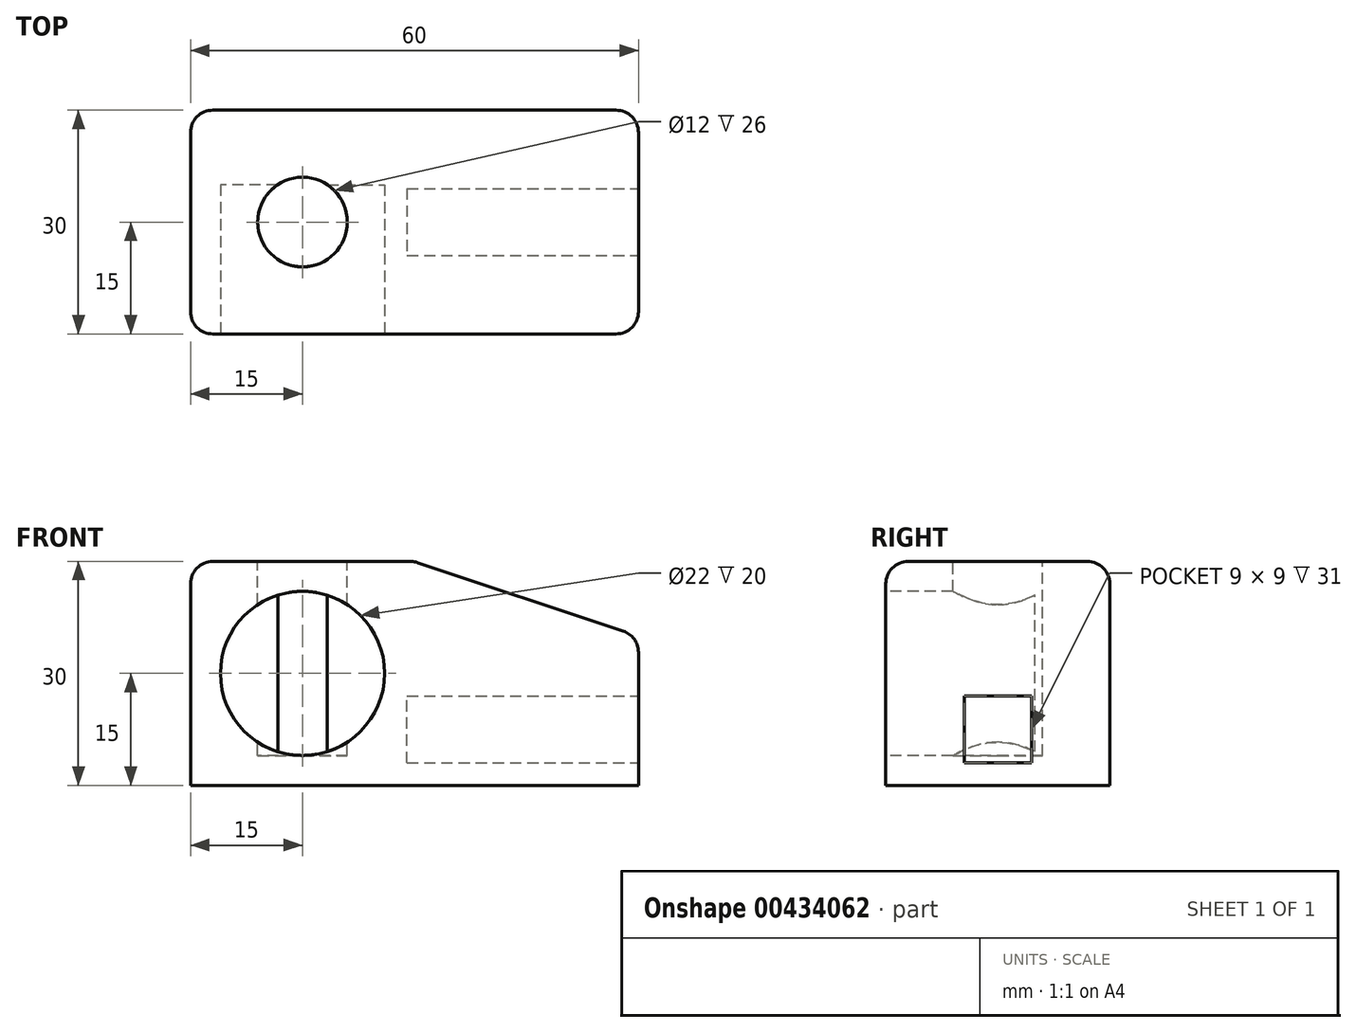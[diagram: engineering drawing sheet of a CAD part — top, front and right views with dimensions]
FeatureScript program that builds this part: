
annotation { "Feature Type Name" : "Feature", "Feature Type Description" : "" }
export const myFeature = defineFeature(function(context is Context, id is Id, definition is map)
    precondition{}
    {
        {
            var Q0;
            Q0=qCreatedBy(makeId("Front.planeOp"),FACE);
            var sketch = newSketch(context, id + "F0", { "sketchPlane" : qUnion([Q0])});
            skLineSegment(sketch, "E0.bottom", {"start": v(30, -15) * mm, "end": v(-30, -15) * mm});
            skLineSegment(sketch, "E0.top", {"start": v(30, 15) * mm, "end": v(-30, 15) * mm});
            skLineSegment(sketch, "E0.left", {"start": v(30, -15) * mm, "end": v(30, 15) * mm});
            skLineSegment(sketch, "E0.right", {"start": v(-30, -15) * mm, "end": v(-30, 15) * mm});
            skPoint(sketch, "E0.middle", {"position": v(0, 0) * mm});
            skSolve(sketch);
        }
        {
            var Q0;
            Q0=makeQuery(id+"F0.imprint","IMPRINT",FACE,{"disambiguationData":[TD([[makeQuery(id+"F0.imprint","IMPRINT",EDGE,{"derivedFrom":sQuery(id+"F0.wireOp",EDGE,"E0.bottom")}),-1.0]])]});
            extrude(context, id + "F1", {"entities" : qUnion([Q0]), "depth" : 30 * mm});
        }
        {
            var Q0;
            Q0=makeQuery(id+"F1.opExtrude","CAP_FACE",FACE,{"disambiguationData":[OSD([sQuery(id+"F0.wireOp",EDGE,"E0.bottom"),sQuery(id+"F0.wireOp",EDGE,"E0.top"),sQuery(id+"F0.wireOp",EDGE,"E0.left"),sQuery(id+"F0.wireOp",EDGE,"E0.right")])],"isStart":false});
            var sketch = newSketch(context, id + "F2", { "sketchPlane" : qUnion([Q0])});
            skLineSegment(sketch, "E1", {"start": v(0, 0) * mm, "end": v(-15, 0) * mm, "construction": true});
            skCircle(sketch, "E2", {"center": v(-15, 0) * mm, "radius": 11 * mm});
            skSolve(sketch);
        }
        {
            var Q0;
            Q0=makeQuery(id+"F2.imprint","IMPRINT",FACE,{"disambiguationData":[TD([[makeQuery(id+"F2.imprint","IMPRINT",EDGE,{"derivedFrom":sQuery(id+"F2.wireOp",EDGE,"E2")}),1.0]])]});
            extrude(context, id + "F3", {"entities" : qUnion([Q0]), "operationType" : NewBodyOperationType.REMOVE, "oppositeDirection" : true, "depth" : 20 * mm});
        }
        {
            var Q0;
            Q0=makeQuery(id+"F1.opExtrude","SWEPT_FACE",FACE,{"disambiguationData":[OSD([sQuery(id+"F0.wireOp",EDGE,"E0.left")])]});
            var sketch = newSketch(context, id + "F4", { "sketchPlane" : qUnion([Q0])});
            skLineSegment(sketch, "E3", {"start": v(-30, -12) * mm, "end": v(0, -12) * mm, "construction": true});
            skLineSegment(sketch, "E4", {"start": v(-15, 15) * mm, "end": v(-15, -15) * mm, "construction": true});
            skLineSegment(sketch, "E5", {"start": v(-19.5, 15) * mm, "end": v(-19.5, -15) * mm, "construction": true});
            skLineSegment(sketch, "E6", {"start": v(-10.5, 15) * mm, "end": v(-10.5, -15) * mm, "construction": true});
            skLineSegment(sketch, "E7", {"start": v(-30, -3) * mm, "end": v(0, -3) * mm, "construction": true});
            skLineSegment(sketch, "E8", {"start": v(-19.5, -12) * mm, "end": v(-19.5, -3) * mm});
            skLineSegment(sketch, "E9", {"start": v(-19.5, -3) * mm, "end": v(-10.5, -3) * mm});
            skLineSegment(sketch, "E10", {"start": v(-10.5, -3) * mm, "end": v(-10.5, -12) * mm});
            skLineSegment(sketch, "E11", {"start": v(-10.5, -12) * mm, "end": v(-19.5, -12) * mm});
            skSolve(sketch);
        }
        {
            var Q0;
            Q0=makeQuery(id+"F4.imprint","IMPRINT",FACE,{"disambiguationData":[TD([[makeQuery(id+"F4.imprint","IMPRINT",EDGE,{"derivedFrom":sQuery(id+"F4.wireOp",EDGE,"E8")}),-1.0]])]});
            extrude(context, id + "F5", {"entities" : qUnion([Q0]), "operationType" : NewBodyOperationType.REMOVE, "oppositeDirection" : true, "depth" : 31 * mm});
        }
        {
            var Q0;
            Q0=makeQuery(id+"F1.opExtrude","SWEPT_FACE",FACE,{"disambiguationData":[OSD([sQuery(id+"F0.wireOp",EDGE,"E0.top")])]});
            var sketch = newSketch(context, id + "F6", { "sketchPlane" : qUnion([Q0])});
            skLineSegment(sketch, "E12", {"start": v(-30, 0) * mm, "end": v(0, -30) * mm, "construction": true});
            skLineSegment(sketch, "E13", {"start": v(0, -30) * mm, "end": v(0, 0) * mm, "construction": true});
            skLineSegment(sketch, "E14", {"start": v(0, 0) * mm, "end": v(-30, -30) * mm, "construction": true});
            skPoint(sketch, "E15", {"position": v(-15, -15) * mm});
            skCircle(sketch, "E16", {"center": v(-15, -15) * mm, "radius": 6 * mm});
            skSolve(sketch);
        }
        {
            var Q0;
            Q0=makeQuery(id+"F6.imprint","IMPRINT",FACE,{"disambiguationData":[TD([[makeQuery(id+"F6.imprint","IMPRINT",EDGE,{"derivedFrom":sQuery(id+"F6.wireOp",EDGE,"E16")}),1.0]])]});
            extrude(context, id + "F7", {"entities" : qUnion([Q0]), "operationType" : NewBodyOperationType.REMOVE, "oppositeDirection" : true, "depth" : 26 * mm});
        }
        {
            var Q0;
            Q0=makeQuery(id+"F1.opExtrude","SWEPT_EDGE",EDGE,{"disambiguationData":[OSD([sQuery(id+"F0.wireOp",EDGE,"E0.top"),sQuery(id+"F0.wireOp",EDGE,"E0.left")])]});
            chamfer(context, id + "F8", {"entities" : qUnion([Q0]), "chamferType" : ChamferType.TWO_OFFSETS, "width1" : 30 * mm, "oppositeDirection" : false, "width2" : 10 * mm, "tangentPropagation" : true});
        }
        {
            var Q0;
            Q0=makeQuery(id+"F1.opExtrude","SWEPT_EDGE",EDGE,{"disambiguationData":[OSD([sQuery(id+"F0.wireOp",EDGE,"E0.top"),sQuery(id+"F0.wireOp",EDGE,"E0.right")])]});
            var Q1;
            Q1=makeQuery(id+"F1.opExtrude","CAP_EDGE",EDGE,{"disambiguationData":[OSD([sQuery(id+"F0.wireOp",EDGE,"E0.top")])],"isStart":true});
            var Q2;
            {var subQ0=sQuery(id+"F0.wireOp",EDGE,"E0.top");Q2=makeQuery(id+"F8.opChamfer","BLEND_EDGE",EDGE,{"blendedFrom":[makeQuery(id+"F1.opExtrude","SWEPT_EDGE",EDGE,{"disambiguationData":[OSD([subQ0,sQuery(id+"F0.wireOp",EDGE,"E0.left")])]}),makeQuery(id+"F1.opExtrude","SWEPT_FACE",FACE,{"disambiguationData":[OSD([subQ0])]})],"blendedInto":[makeQuery(id+"F1.opExtrude","SWEPT_FACE",FACE,{"disambiguationData":[OSD([subQ0])]})]});}
            var Q3;
            {var subQ0=sQuery(id+"F0.wireOp",EDGE,"E0.left");Q3=makeQuery(id+"F8.opChamfer","BLEND_EDGE",EDGE,{"blendedFrom":[makeQuery(id+"F1.opExtrude","SWEPT_EDGE",EDGE,{"disambiguationData":[OSD([sQuery(id+"F0.wireOp",EDGE,"E0.top"),subQ0])]}),makeQuery(id+"F1.opExtrude","SWEPT_FACE",FACE,{"disambiguationData":[OSD([subQ0])]})],"blendedInto":[makeQuery(id+"F1.opExtrude","SWEPT_FACE",FACE,{"disambiguationData":[OSD([subQ0])]})]});}
            var Q4;
            Q4=makeQuery(id+"F1.opExtrude","CAP_EDGE",EDGE,{"disambiguationData":[OSD([sQuery(id+"F0.wireOp",EDGE,"E0.top")])],"isStart":false});
            var Q5;
            {var subQ0=sQuery(id+"F0.wireOp",EDGE,"E0.left");var subQ1=sQuery(id+"F0.wireOp",EDGE,"E0.top");Q5=makeQuery(id+"F8.opChamfer","BLEND_EDGE",EDGE,{"blendedFrom":[makeQuery(id+"F1.opExtrude","SWEPT_EDGE",EDGE,{"disambiguationData":[OSD([subQ1,subQ0])]}),makeQuery(id+"F1.opExtrude","CAP_FACE",FACE,{"disambiguationData":[OSD([sQuery(id+"F0.wireOp",EDGE,"E0.bottom"),subQ1,subQ0,sQuery(id+"F0.wireOp",EDGE,"E0.right")])],"isStart":false})],"blendedInto":[makeQuery(id+"F1.opExtrude","CAP_FACE",FACE,{"disambiguationData":[OSD([sQuery(id+"F0.wireOp",EDGE,"E0.bottom"),subQ1,subQ0,sQuery(id+"F0.wireOp",EDGE,"E0.right")])],"isStart":false})]});}
            var Q6;
            {var subQ0=sQuery(id+"F0.wireOp",EDGE,"E0.left");var subQ1=sQuery(id+"F0.wireOp",EDGE,"E0.top");Q6=makeQuery(id+"F8.opChamfer","BLEND_EDGE",EDGE,{"blendedFrom":[makeQuery(id+"F1.opExtrude","SWEPT_EDGE",EDGE,{"disambiguationData":[OSD([subQ1,subQ0])]}),makeQuery(id+"F1.opExtrude","CAP_FACE",FACE,{"disambiguationData":[OSD([sQuery(id+"F0.wireOp",EDGE,"E0.bottom"),subQ1,subQ0,sQuery(id+"F0.wireOp",EDGE,"E0.right")])],"isStart":true})],"blendedInto":[makeQuery(id+"F1.opExtrude","CAP_FACE",FACE,{"disambiguationData":[OSD([sQuery(id+"F0.wireOp",EDGE,"E0.bottom"),subQ1,subQ0,sQuery(id+"F0.wireOp",EDGE,"E0.right")])],"isStart":true})]});}
            var Q7;
            Q7=makeQuery(id+"F1.opExtrude","CAP_EDGE",EDGE,{"disambiguationData":[OSD([sQuery(id+"F0.wireOp",EDGE,"E0.left")])],"isStart":false});
            var Q8;
            Q8=makeQuery(id+"F1.opExtrude","CAP_EDGE",EDGE,{"disambiguationData":[OSD([sQuery(id+"F0.wireOp",EDGE,"E0.left")])],"isStart":true});
            var Q9;
            Q9=makeQuery(id+"F1.opExtrude","CAP_EDGE",EDGE,{"disambiguationData":[OSD([sQuery(id+"F0.wireOp",EDGE,"E0.right")])],"isStart":true});
            var Q10;
            Q10=makeQuery(id+"F1.opExtrude","CAP_EDGE",EDGE,{"disambiguationData":[OSD([sQuery(id+"F0.wireOp",EDGE,"E0.right")])],"isStart":false});
            fillet(context, id + "F9", {"entities" : qUnion([Q0, Q1, Q2, Q3, Q4, Q5, Q6, Q7, Q8, Q9, Q10]), "radius" : 3 * mm, "tangentPropagation" : true, "allowEdgeOverflow" : false});
        }
    });
